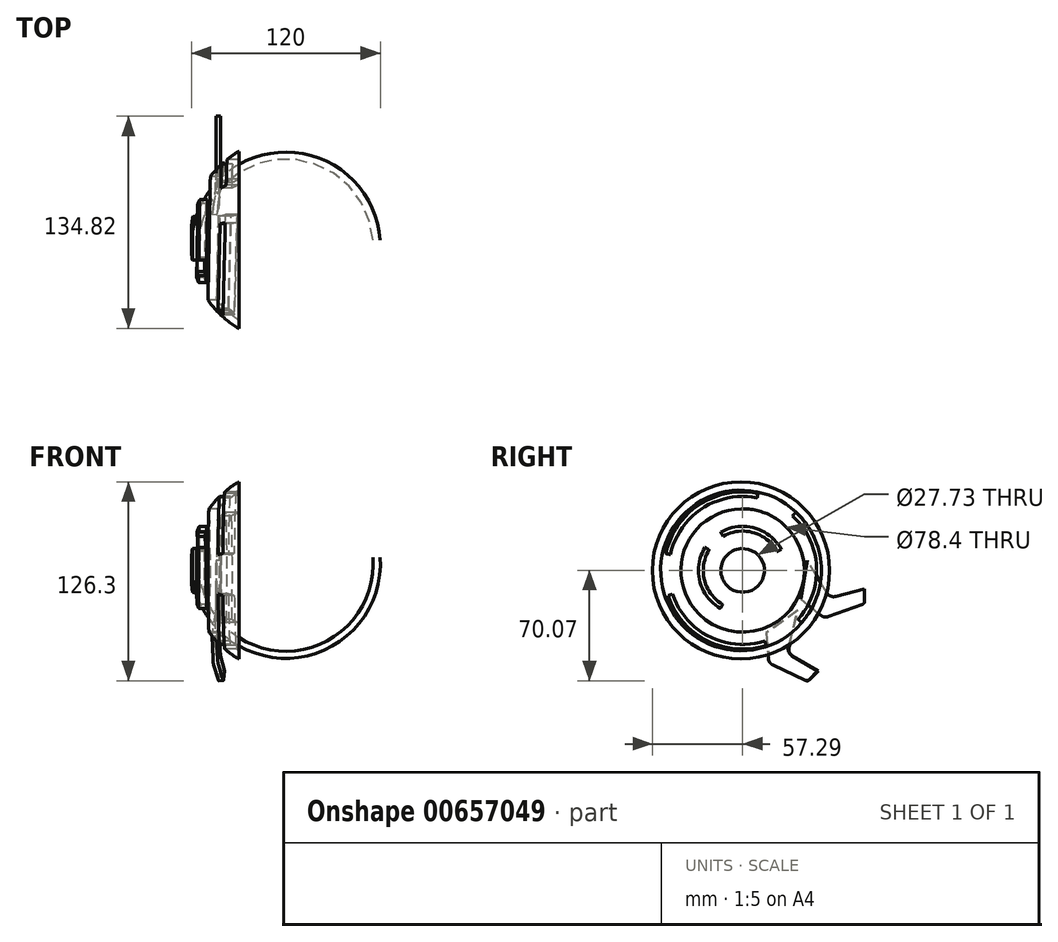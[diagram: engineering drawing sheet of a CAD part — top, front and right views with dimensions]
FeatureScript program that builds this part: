
annotation { "Feature Type Name" : "Feature", "Feature Type Description" : "" }
export const myFeature = defineFeature(function(context is Context, id is Id, definition is map)
    precondition{}
    {
        {
            var Q0;
            Q0=qCreatedBy(makeId("Right.planeOp"),FACE);
            var sketch = newSketch(context, id + "F0", { "sketchPlane" : qUnion([Q0])});
            skCircle(sketch, "E0", {"center": v(-56.27, 47.63) * mm, "radius": 55.63 * mm});
            skSolve(sketch);
        }
        {
            var Q0;
            Q0 = qSketchRegion(id + "F0", true);
            extrude(context, id + "F1", {"entities" : qUnion([Q0]), "depth" : 30 * mm, "offsetDistance" : 25.4 * mm});
        }
        {
            var Q0;
            Q0=makeQuery(id+"F1.opExtrude","CAP_EDGE",EDGE,{"disambiguationData":[OSD([sQuery(id+"F0.wireOp",EDGE,"E0")])],"isStart":true});
            fillet(context, id + "F2", {"entities" : qUnion([Q0]), "radius" : 55 * mm, "tangentPropagation" : true, "allowEdgeOverflow" : false});
        }
        {
            var Q0;
            Q0=qCreatedBy(makeId("Top.planeOp"),FACE);
            var sketch = newSketch(context, id + "F3", { "sketchPlane" : qUnion([Q0])});
            skArc(sketch, "E1", {"start": v(24.47, 69.37) * mm, "mid": v(31.39, 36.94) * mm, "end": v(54.47, 13.14) * mm});
            skLineSegment(sketch, "E2", {"start": v(24.47, 69.37) * mm, "end": v(54.47, 69.37) * mm, "construction": true});
            skArc(sketch, "E3.0", {"start": v(28.98, 69.37) * mm, "mid": v(34.68, 40.36) * mm, "end": v(54.47, 18.4) * mm});
            skLineSegment(sketch, "E4", {"start": v(28.98, 69.37) * mm, "end": v(24.47, 69.37) * mm});
            skLineSegment(sketch, "E5", {"start": v(54.47, 18.4) * mm, "end": v(54.47, 13.14) * mm});
            skSolve(sketch);
        }
        {
            var Q0;
            Q0=makeQuery(id+"F3.imprint","IMPRINT",FACE,{"disambiguationData":[TD([[makeQuery(id+"F3.imprint","IMPRINT",EDGE,{"derivedFrom":sQuery(id+"F3.wireOp",EDGE,"E1")}),1.0]])]});
            var Q1;
            Q1=sQuery(id+"F3.wireOp",EDGE,"E2");
            revolve(context, id + "F4", {"entities" : qUnion([Q0]), "axis" : qUnion([Q1]), "revolveType" : RevolveType.FULL});
        }
        {
            var Q0;
            Q0=qCreatedBy(makeId("Right.planeOp"),FACE);
            var sketch = newSketch(context, id + "F5", { "sketchPlane" : qUnion([Q0])});
            skLineSegment(sketch, "E6", {"start": v(130.62, -13.51) * mm, "end": v(143.33, -23.92) * mm});
            skLineSegment(sketch, "E7", {"start": v(148.2, -24.76) * mm, "end": v(169.87, -16.92) * mm});
            skLineSegment(sketch, "E8", {"start": v(171.2, -15.04) * mm, "end": v(171.2, -7.04) * mm});
            skLineSegment(sketch, "E9", {"start": v(171.2, -7.04) * mm, "end": v(152.8, -11.93) * mm});
            skLineSegment(sketch, "E10", {"start": v(147.22, -9.67) * mm, "end": v(134.9, 10.9) * mm});
            skLineSegment(sketch, "E11", {"start": v(134.9, 10.9) * mm, "end": v(130.62, -13.51) * mm});
            skPoint(sketch, "E12.visualSharp", {"position": v(145.53, -25.72) * mm});
            skArc(sketch, "E12.filletArc", {"start": v(143.33, -23.92) * mm, "mid": v(145.66, -24.98) * mm, "end": v(148.2, -24.76) * mm});
            skPoint(sketch, "E13.visualSharp", {"position": v(149.16, -12.9) * mm});
            skArc(sketch, "E13.filletArc", {"start": v(147.22, -9.67) * mm, "mid": v(149.63, -11.74) * mm, "end": v(152.8, -11.93) * mm});
            skPoint(sketch, "E14.visualSharp", {"position": v(171.2, -16.45) * mm});
            skArc(sketch, "E14.filletArc", {"start": v(169.87, -16.92) * mm, "mid": v(170.83, -16.2) * mm, "end": v(171.2, -15.04) * mm});
            skLineSegment(sketch, "E15", {"start": v(138.4, 101.9) * mm, "end": v(151.1, 91.48) * mm});
            skLineSegment(sketch, "E16", {"start": v(155.97, 90.65) * mm, "end": v(177.64, 98.48) * mm});
            skLineSegment(sketch, "E17", {"start": v(178.96, 100.36) * mm, "end": v(178.96, 108.36) * mm});
            skLineSegment(sketch, "E18", {"start": v(178.96, 108.36) * mm, "end": v(160.57, 103.47) * mm});
            skLineSegment(sketch, "E19", {"start": v(155, 105.74) * mm, "end": v(142.68, 126.31) * mm});
            skLineSegment(sketch, "E20", {"start": v(142.68, 126.31) * mm, "end": v(138.4, 101.9) * mm});
            skPoint(sketch, "E21.visualSharp", {"position": v(153.3, 89.68) * mm});
            skArc(sketch, "E21.filletArc", {"start": v(151.1, 91.48) * mm, "mid": v(153.43, 90.42) * mm, "end": v(155.97, 90.65) * mm});
            skPoint(sketch, "E22.visualSharp", {"position": v(156.93, 102.5) * mm});
            skArc(sketch, "E22.filletArc", {"start": v(155, 105.74) * mm, "mid": v(157.4, 103.67) * mm, "end": v(160.57, 103.47) * mm});
            skPoint(sketch, "E23.visualSharp", {"position": v(178.96, 98.96) * mm});
            skArc(sketch, "E23.filletArc", {"start": v(177.64, 98.48) * mm, "mid": v(178.6, 99.21) * mm, "end": v(178.96, 100.36) * mm});
            skSolve(sketch);
        }
        {
            var Q0;
            Q0=qCreatedBy(makeId("Right.planeOp"),FACE);
            var sketch = newSketch(context, id + "F6", { "sketchPlane" : qUnion([Q0])});
            skArc(sketch, "E24", {"start": v(104.16, 36.9) * mm, "mid": v(120.36, 2.67) * mm, "end": v(107.9, -33.1) * mm});
            skArc(sketch, "E25", {"start": v(85.46, -47.69) * mm, "mid": v(47.78, -44.58) * mm, "end": v(23.05, -15.98) * mm});
            skArc(sketch, "E26", {"start": v(21.6, 10.76) * mm, "mid": v(43.1, 41.87) * mm, "end": v(80.21, 49.03) * mm});
            skArc(sketch, "E27.0", {"start": v(84.55, -44.83) * mm, "mid": v(49.14, -41.9) * mm, "end": v(25.9, -15.02) * mm});
            skArc(sketch, "E28.0", {"start": v(24.53, 10.12) * mm, "mid": v(44.73, 39.35) * mm, "end": v(79.63, 46.1) * mm});
            skArc(sketch, "E29.0", {"start": v(102.14, 34.7) * mm, "mid": v(117.36, 2.51) * mm, "end": v(105.66, -31.1) * mm});
            skLineSegment(sketch, "E30", {"start": v(23.05, -15.98) * mm, "end": v(25.9, -15.02) * mm});
            skLineSegment(sketch, "E31", {"start": v(84.55, -44.83) * mm, "end": v(85.46, -47.69) * mm});
            skLineSegment(sketch, "E32", {"start": v(24.53, 10.12) * mm, "end": v(21.6, 10.76) * mm});
            skLineSegment(sketch, "E33", {"start": v(80.21, 49.03) * mm, "end": v(79.63, 46.1) * mm});
            skLineSegment(sketch, "E34", {"start": v(104.16, 36.9) * mm, "end": v(102.14, 34.7) * mm});
            skLineSegment(sketch, "E35", {"start": v(105.66, -31.1) * mm, "end": v(107.9, -33.1) * mm});
            skCircle(sketch, "E36", {"center": v(70.43, 0) * mm, "radius": 39.2 * mm});
            skCircle(sketch, "E37.0", {"center": v(70.43, 0) * mm, "radius": 36.2 * mm});
            skArc(sketch, "E38", {"start": v(69.86, -28) * mm, "mid": v(90.03, -20) * mm, "end": v(98.43, 0) * mm});
            skArc(sketch, "E39", {"start": v(56.25, -24.15) * mm, "mid": v(43.26, -6.77) * mm, "end": v(46.58, 14.67) * mm});
            skArc(sketch, "E40", {"start": v(56.52, 24.3) * mm, "mid": v(78.05, 26.94) * mm, "end": v(95, 13.41) * mm});
            skArc(sketch, "E41.0", {"start": v(58, 21.7) * mm, "mid": v(77.23, 24.06) * mm, "end": v(92.37, 11.98) * mm});
            skArc(sketch, "E42.0", {"start": v(69.92, -25) * mm, "mid": v(87.93, -17.86) * mm, "end": v(95.43, 0) * mm});
            skArc(sketch, "E43.0", {"start": v(57.77, -21.56) * mm, "mid": v(46.17, -6.05) * mm, "end": v(49.13, 13.1) * mm});
            skLineSegment(sketch, "E44", {"start": v(57.77, -21.56) * mm, "end": v(56.25, -24.15) * mm});
            skLineSegment(sketch, "E45", {"start": v(49.13, 13.1) * mm, "end": v(46.58, 14.67) * mm});
            skLineSegment(sketch, "E46", {"start": v(58, 21.7) * mm, "end": v(56.52, 24.3) * mm});
            skLineSegment(sketch, "E47", {"start": v(95, 13.41) * mm, "end": v(92.37, 11.98) * mm});
            skLineSegment(sketch, "E48", {"start": v(95.43, 0) * mm, "end": v(98.43, 0) * mm});
            skLineSegment(sketch, "E49", {"start": v(69.86, -28) * mm, "end": v(69.92, -25) * mm});
            skCircle(sketch, "E50", {"center": v(70.43, 0) * mm, "radius": 16.86 * mm});
            skCircle(sketch, "E51", {"center": v(70.43, 0) * mm, "radius": 13.86 * mm});
            skSolve(sketch);
        }
        {
            var Q0;
            Q0 = qSketchRegion(id + "F6", true);
            var Q1;
            Q1=makeQuery(id+"F6.imprint","IMPRINT",FACE,{"disambiguationData":[TD([[makeQuery(id+"F6.imprint","IMPRINT",EDGE,{"derivedFrom":sQuery(id+"F6.wireOp",EDGE,"E39")}),-1.0]])]});
            var Q2;
            Q2=makeQuery(id+"F6.imprint","IMPRINT",FACE,{"disambiguationData":[TD([[makeQuery(id+"F6.imprint","IMPRINT",EDGE,{"derivedFrom":sQuery(id+"F6.wireOp",EDGE,"E50")}),1.0]])]});
            var Q3;
            Q3=makeQuery(id+"F6.imprint","IMPRINT",FACE,{"disambiguationData":[TD([[makeQuery(id+"F6.imprint","IMPRINT",EDGE,{"derivedFrom":sQuery(id+"F6.wireOp",EDGE,"E40")}),-1.0]])]});
            var Q4;
            Q4=makeQuery(id+"F6.imprint","IMPRINT",FACE,{"disambiguationData":[TD([[makeQuery(id+"F6.imprint","IMPRINT",EDGE,{"derivedFrom":sQuery(id+"F6.wireOp",EDGE,"E38")}),1.0]])]});
            extrude(context, id + "F7", {"entities" : qUnion([Q0, Q1, Q2, Q3, Q4]), "operationType" : NewBodyOperationType.REMOVE, "depth" : 100 * mm, "offsetDistance" : 25 * mm});
        }
        {
            var Q0;
            Q0 = qSketchRegion(id + "F5", true);
            extrude(context, id + "F8", {"entities" : qUnion([Q0]), "depth" : 3 * mm, "offsetDistance" : 25 * mm});
        }
        {
            var Q0;
            Q0=makeQuery(id+"F8.opExtrude","SWEPT_BODY",BODY,{"disambiguationData":[OSD([sQuery(id+"F5.wireOp",EDGE,"E6"),sQuery(id+"F5.wireOp",EDGE,"E7"),sQuery(id+"F5.wireOp",EDGE,"E8"),sQuery(id+"F5.wireOp",EDGE,"E9"),sQuery(id+"F5.wireOp",EDGE,"E10"),sQuery(id+"F5.wireOp",EDGE,"E11"),sQuery(id+"F5.wireOp",EDGE,"E12.filletArc"),sQuery(id+"F5.wireOp",EDGE,"E13.filletArc"),sQuery(id+"F5.wireOp",EDGE,"E14.filletArc")])]});
            var Q1;
            Q1=makeQuery(id+"F8.opExtrude","CAP_VERTEX",VERTEX,{"disambiguationData":[OSD([sQuery(id+"F5.wireOp",EDGE,"E6"),sQuery(id+"F5.wireOp",EDGE,"E11")])],"isStart":false});
            var Q2;
            Q2=makeQuery(id+"F8.opExtrude","CAP_EDGE",EDGE,{"disambiguationData":[OSD([sQuery(id+"F5.wireOp",EDGE,"E11")])],"isStart":true});
            transform(context, id + "F9", {"entities" : qUnion([Q0]), "transformType" : TransformType.ROTATION, "transformAxis" : qUnion([Q2]), "angle" : 7.9 * degree, "makeCopy" : false});
        }
        {
            var Q0;
            Q0=makeQuery(id+"F8.opExtrude","SWEPT_BODY",BODY,{"disambiguationData":[OSD([sQuery(id+"F5.wireOp",EDGE,"E6"),sQuery(id+"F5.wireOp",EDGE,"E7"),sQuery(id+"F5.wireOp",EDGE,"E8"),sQuery(id+"F5.wireOp",EDGE,"E9"),sQuery(id+"F5.wireOp",EDGE,"E10"),sQuery(id+"F5.wireOp",EDGE,"E11"),sQuery(id+"F5.wireOp",EDGE,"E12.filletArc"),sQuery(id+"F5.wireOp",EDGE,"E13.filletArc"),sQuery(id+"F5.wireOp",EDGE,"E14.filletArc")])]});
            transform(context, id + "F10", {"entities" : qUnion([Q0]), "transformType" : TransformType.TRANSLATION_3D, "dx" : 38.4 * mm, "dy" : -25.9 * mm, "dz" : -53 * mm, "makeCopy" : false});
        }
        {
            var Q0;
            Q0=makeQuery(id+"F8.opExtrude","SWEPT_BODY",BODY,{"disambiguationData":[OSD([sQuery(id+"F5.wireOp",EDGE,"E6"),sQuery(id+"F5.wireOp",EDGE,"E7"),sQuery(id+"F5.wireOp",EDGE,"E8"),sQuery(id+"F5.wireOp",EDGE,"E9"),sQuery(id+"F5.wireOp",EDGE,"E10"),sQuery(id+"F5.wireOp",EDGE,"E11"),sQuery(id+"F5.wireOp",EDGE,"E12.filletArc"),sQuery(id+"F5.wireOp",EDGE,"E13.filletArc"),sQuery(id+"F5.wireOp",EDGE,"E14.filletArc")])]});
            var Q1;
            Q1=makeQuery(id+"F8.opExtrude","SWEPT_EDGE",EDGE,{"disambiguationData":[OSD([sQuery(id+"F5.wireOp",EDGE,"E10"),sQuery(id+"F5.wireOp",EDGE,"E11")])]});
            transform(context, id + "F11", {"entities" : qUnion([Q0]), "transformType" : TransformType.ROTATION, "transformAxis" : qUnion([Q1]), "angle" : 45 * degree, "makeCopy" : false});
        }
        {
            var Q0;
            Q0=makeQuery(id+"F8.opExtrude","SWEPT_BODY",BODY,{"disambiguationData":[OSD([sQuery(id+"F5.wireOp",EDGE,"E6"),sQuery(id+"F5.wireOp",EDGE,"E7"),sQuery(id+"F5.wireOp",EDGE,"E8"),sQuery(id+"F5.wireOp",EDGE,"E9"),sQuery(id+"F5.wireOp",EDGE,"E10"),sQuery(id+"F5.wireOp",EDGE,"E11"),sQuery(id+"F5.wireOp",EDGE,"E12.filletArc"),sQuery(id+"F5.wireOp",EDGE,"E13.filletArc"),sQuery(id+"F5.wireOp",EDGE,"E14.filletArc")])]});
            transform(context, id + "F12", {"entities" : qUnion([Q0]), "transformType" : TransformType.TRANSLATION_3D, "dx" : 1.4 * mm, "dy" : -3.3 * mm, "dz" : 16.6 * mm, "makeCopy" : false});
        }
        {
            var Q0;
            Q0=makeQuery(id+"F8.opExtrude","SWEPT_BODY",BODY,{"disambiguationData":[OSD([sQuery(id+"F5.wireOp",EDGE,"E15"),sQuery(id+"F5.wireOp",EDGE,"E16"),sQuery(id+"F5.wireOp",EDGE,"E17"),sQuery(id+"F5.wireOp",EDGE,"E18"),sQuery(id+"F5.wireOp",EDGE,"E19"),sQuery(id+"F5.wireOp",EDGE,"E20"),sQuery(id+"F5.wireOp",EDGE,"E21.filletArc"),sQuery(id+"F5.wireOp",EDGE,"E22.filletArc"),sQuery(id+"F5.wireOp",EDGE,"E23.filletArc")])]});
            transform(context, id + "F13", {"entities" : qUnion([Q0]), "transformType" : TransformType.TRANSLATION_3D, "dx" : 40 * mm, "dy" : -31 * mm, "dz" : -120 * mm, "makeCopy" : false});
        }
        {
            var Q0;
            Q0=makeQuery(id+"F1.opExtrude","SWEPT_BODY",BODY,{"disambiguationData":[OSD([sQuery(id+"F0.wireOp",EDGE,"E0")])]});
            deleteBodies(context, id + "F14", {"entities" : qUnion([Q0])});
        }
    });
